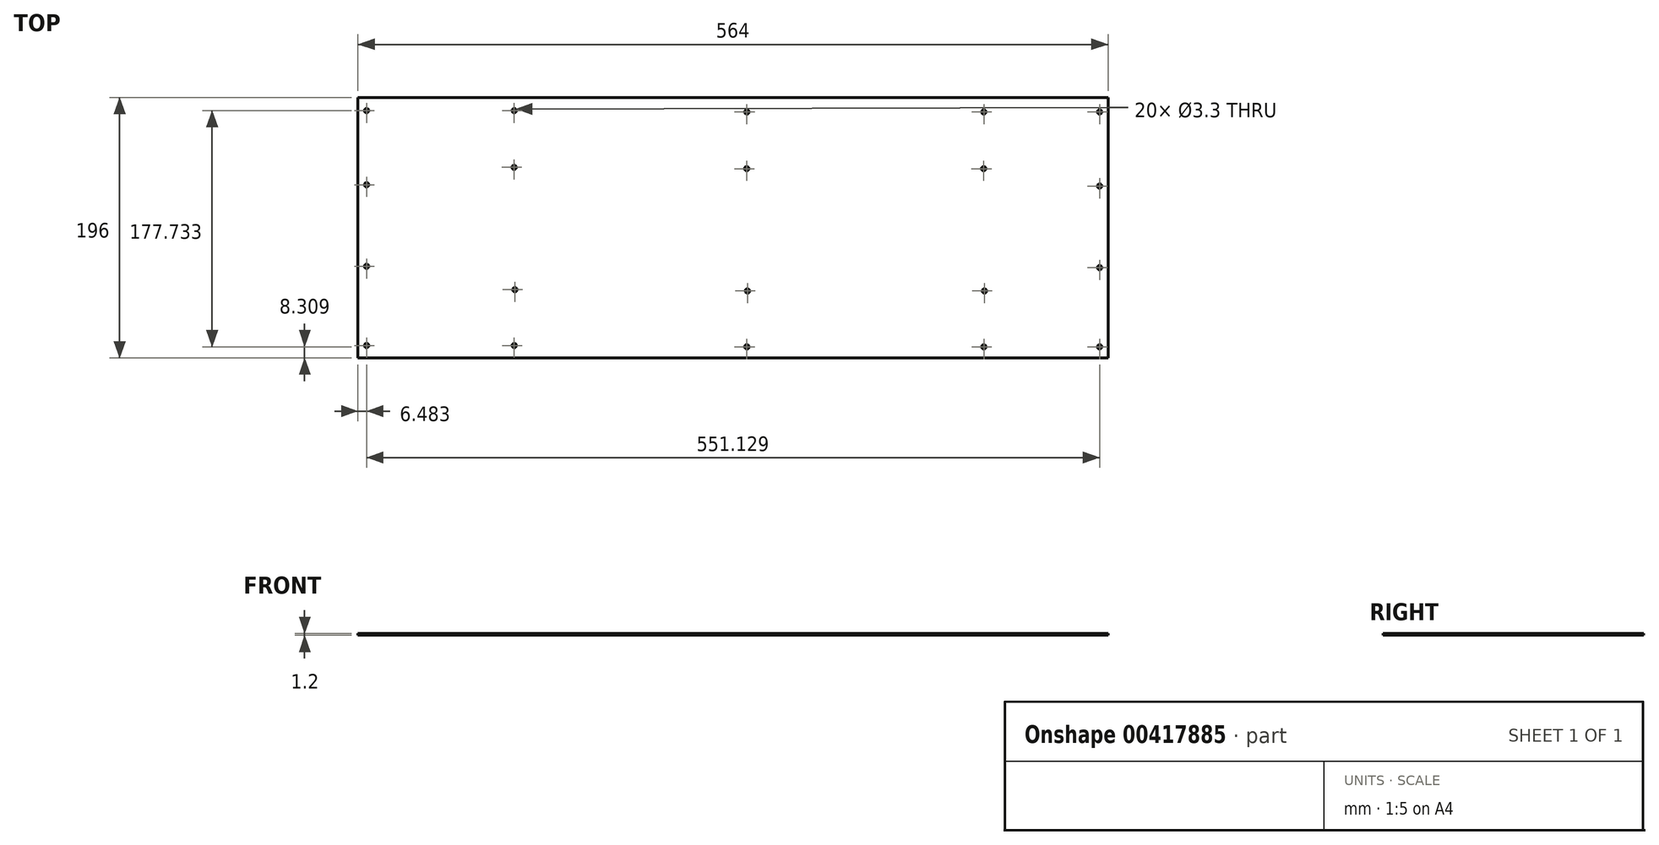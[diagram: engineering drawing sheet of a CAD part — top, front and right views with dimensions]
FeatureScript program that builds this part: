
annotation { "Feature Type Name" : "Feature", "Feature Type Description" : "" }
export const myFeature = defineFeature(function(context is Context, id is Id, definition is map)
    precondition{}
    {
        {
            var Q0;
            Q0=qCreatedBy(makeId("Top.planeOp"),FACE);
            var sketch = newSketch(context, id + "F0", { "sketchPlane" : qUnion([Q0])});
            skLineSegment(sketch, "E0.bottom", {"start": v(-468.08, 131.3) * mm, "end": v(95.92, 131.3) * mm});
            skLineSegment(sketch, "E0.top", {"start": v(-468.08, -64.7) * mm, "end": v(95.92, -64.7) * mm});
            skLineSegment(sketch, "E0.left", {"start": v(-468.08, 131.3) * mm, "end": v(-468.08, -64.7) * mm});
            skLineSegment(sketch, "E0.right", {"start": v(95.92, 131.3) * mm, "end": v(95.92, -64.7) * mm});
            skPoint(sketch, "E1", {"position": v(-461.6, 121.34) * mm});
            skPoint(sketch, "E2", {"position": v(-461.6, -55.4) * mm});
            skPoint(sketch, "E3", {"position": v(-461.6, 4.2) * mm});
            skPoint(sketch, "E4", {"position": v(-461.6, 65.58) * mm});
            skPoint(sketch, "E5", {"position": v(-350.6, 121.34) * mm});
            skPoint(sketch, "E6", {"position": v(-350.6, -55.4) * mm});
            skPoint(sketch, "E7", {"position": v(-350.14, -13.37) * mm});
            skPoint(sketch, "E8", {"position": v(-350.7, 78.66) * mm});
            skPoint(sketch, "E9", {"position": v(-175.71, 120.35) * mm});
            skPoint(sketch, "E10", {"position": v(-175.71, -56.4) * mm});
            skPoint(sketch, "E11", {"position": v(-175.26, -14.36) * mm});
            skPoint(sketch, "E12", {"position": v(-175.8, 77.67) * mm});
            skPoint(sketch, "E13", {"position": v(2.49, 120.35) * mm});
            skPoint(sketch, "E14", {"position": v(2.49, -56.4) * mm});
            skPoint(sketch, "E15", {"position": v(2.94, -14.36) * mm});
            skPoint(sketch, "E16", {"position": v(2.4, 77.67) * mm});
            skPoint(sketch, "E17", {"position": v(89.53, 120.35) * mm});
            skPoint(sketch, "E18", {"position": v(89.53, -56.4) * mm});
            skPoint(sketch, "E19", {"position": v(89.53, 3.2) * mm});
            skPoint(sketch, "E20", {"position": v(89.53, 64.59) * mm});
            skSolve(sketch);
        }
        {
            var Q0;
            Q0 = qSketchRegion(id + "F0", true);
            extrude(context, id + "F1", {"entities" : qUnion([Q0]), "depth" : 1.2 * mm});
        }
        {
            var Q0;
            Q0=sQuery(id+"F0.wireOp",VERTEX,"E1");
            var Q1;
            Q1=makeQuery(id+"F1.opExtrude","SWEPT_BODY",BODY,{"disambiguationData":[OSD([sQuery(id+"F0.wireOp",EDGE,"E0.bottom"),sQuery(id+"F0.wireOp",EDGE,"E0.top"),sQuery(id+"F0.wireOp",EDGE,"E0.left"),sQuery(id+"F0.wireOp",EDGE,"E0.right")])]});
            hole(context, id + "F2", {"style" : HoleStyle.SIMPLE, "endStyle" : HoleEndStyle.BLIND, "oppositeDirection" : true, "holeDiameter" : 3.3 * mm, "holeDepth" : 5 * mm, "isTappedThrough" : true, "tappedDepth" : 12 * mm, "tapClearance" : 3, "locations" : qUnion([Q0]), "scope" : qUnion([Q1])});
        }
        {
            var Q0;
            Q0=sQuery(id+"F0.wireOp",VERTEX,"E4");
            var Q1;
            Q1=sQuery(id+"F0.wireOp",VERTEX,"E3");
            var Q2;
            Q2=sQuery(id+"F0.wireOp",VERTEX,"E2");
            var Q3;
            Q3=sQuery(id+"F0.wireOp",VERTEX,"E6");
            var Q4;
            Q4=sQuery(id+"F0.wireOp",VERTEX,"E7");
            var Q5;
            Q5=sQuery(id+"F0.wireOp",VERTEX,"E8");
            var Q6;
            Q6=sQuery(id+"F0.wireOp",VERTEX,"E5");
            var Q7;
            Q7=sQuery(id+"F0.wireOp",VERTEX,"E9");
            var Q8;
            Q8=sQuery(id+"F0.wireOp",VERTEX,"E12");
            var Q9;
            Q9=sQuery(id+"F0.wireOp",VERTEX,"E11");
            var Q10;
            Q10=sQuery(id+"F0.wireOp",VERTEX,"E10");
            var Q11;
            Q11=sQuery(id+"F0.wireOp",VERTEX,"E14");
            var Q12;
            Q12=sQuery(id+"F0.wireOp",VERTEX,"E15");
            var Q13;
            Q13=sQuery(id+"F0.wireOp",VERTEX,"E16");
            var Q14;
            Q14=sQuery(id+"F0.wireOp",VERTEX,"E13");
            var Q15;
            Q15=sQuery(id+"F0.wireOp",VERTEX,"E17");
            var Q16;
            Q16=sQuery(id+"F0.wireOp",VERTEX,"E20");
            var Q17;
            Q17=sQuery(id+"F0.wireOp",VERTEX,"E19");
            var Q18;
            Q18=sQuery(id+"F0.wireOp",VERTEX,"E18");
            var Q19;
            Q19=makeQuery(id+"F1.opExtrude","SWEPT_BODY",BODY,{"disambiguationData":[OSD([sQuery(id+"F0.wireOp",EDGE,"E0.bottom"),sQuery(id+"F0.wireOp",EDGE,"E0.top"),sQuery(id+"F0.wireOp",EDGE,"E0.left"),sQuery(id+"F0.wireOp",EDGE,"E0.right")])]});
            hole(context, id + "F3", {"style" : HoleStyle.SIMPLE, "endStyle" : HoleEndStyle.BLIND, "oppositeDirection" : true, "holeDiameter" : 3.3 * mm, "holeDepth" : 5 * mm, "isTappedThrough" : true, "tappedDepth" : 12 * mm, "tapClearance" : 3, "locations" : qUnion([Q0, Q1, Q2, Q3, Q4, Q5, Q6, Q7, Q8, Q9, Q10, Q11, Q12, Q13, Q14, Q15, Q16, Q17, Q18]), "scope" : qUnion([Q19])});
        }
    });
